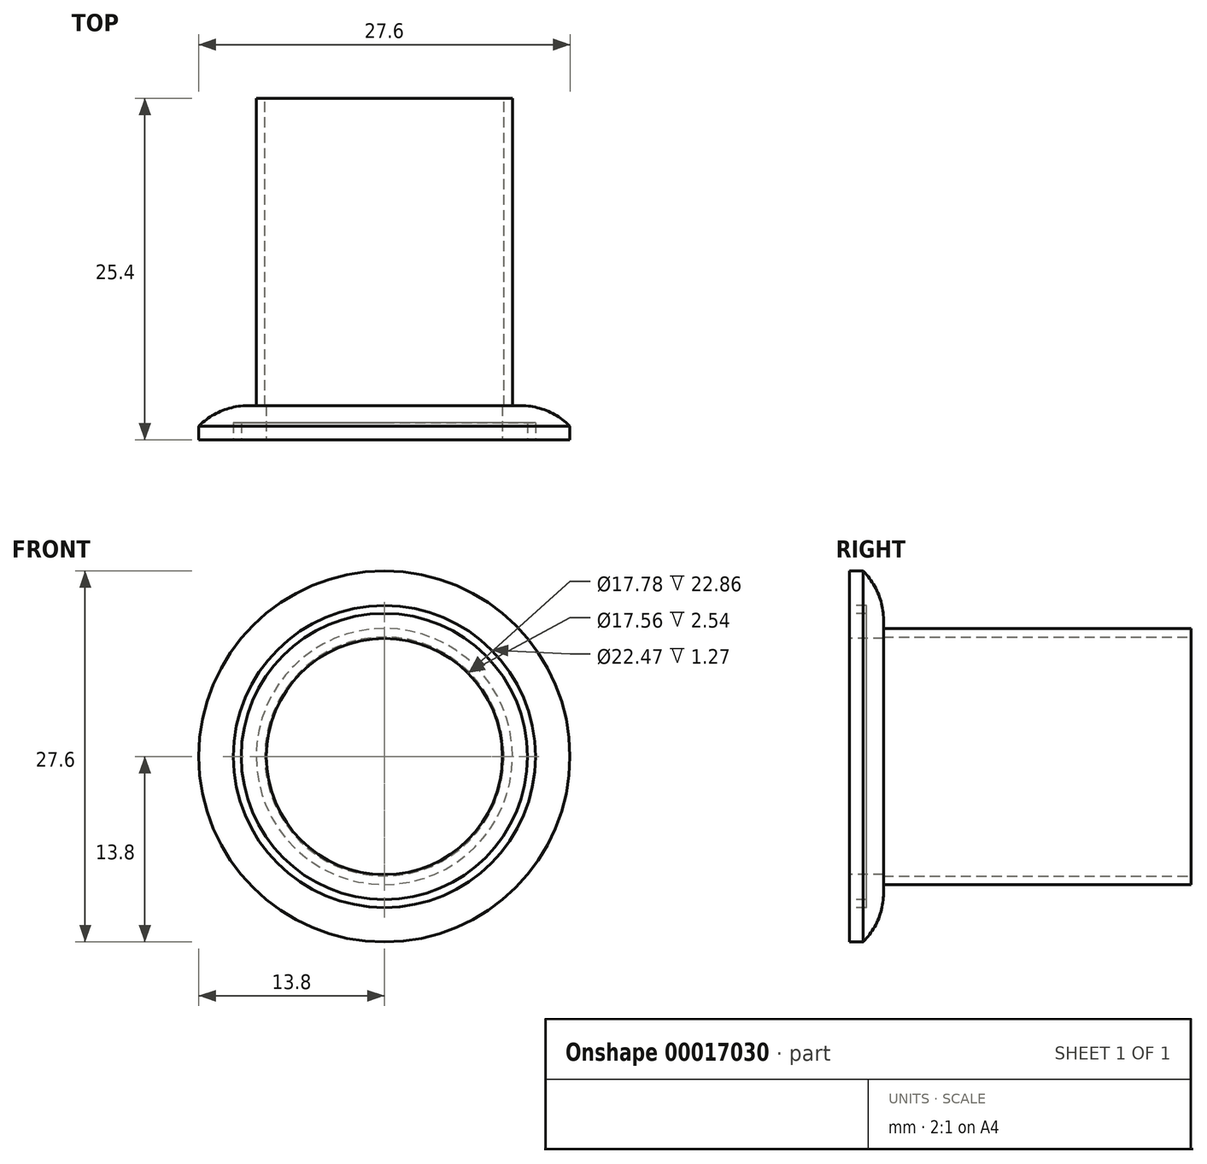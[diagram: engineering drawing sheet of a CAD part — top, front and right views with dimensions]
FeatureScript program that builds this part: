
annotation { "Feature Type Name" : "Feature", "Feature Type Description" : "" }
export const myFeature = defineFeature(function(context is Context, id is Id, definition is map)
    precondition{}
    {
        {
            var Q0;
            Q0=qCreatedBy(makeId("Front.planeOp"),FACE);
            var sketch = newSketch(context, id + "F0", { "sketchPlane" : qUnion([Q0])});
            skCircle(sketch, "E0", {"center": v(0, 0) * mm, "radius": 9.53 * mm});
            skCircle(sketch, "E1", {"center": v(0, 0) * mm, "radius": 8.9 * mm});
            skSolve(sketch);
        }
        {
            var Q0;
            Q0 = qSketchRegion(id + "F0", true);
            extrude(context, id + "F1", {"entities" : qUnion([Q0]), "depth" : 25.4 * mm});
        }
        {
            var Q0;
            Q0=makeQuery(id+"F1.opExtrude","CAP_FACE",FACE,{"disambiguationData":[OSD([sQuery(id+"F0.wireOp",EDGE,"E0"),sQuery(id+"F0.wireOp",EDGE,"E1")])],"isStart":false});
            var sketch = newSketch(context, id + "F2", { "sketchPlane" : qUnion([Q0])});
            skCircle(sketch, "E2", {"center": v(0, 0) * mm, "radius": 13.8 * mm});
            skCircle(sketch, "E3", {"center": v(0, 0) * mm, "radius": 8.78 * mm});
            skSolve(sketch);
        }
        {
            var Q0;
            Q0 = qSketchRegion(id + "F2", true);
            extrude(context, id + "F3", {"entities" : qUnion([Q0]), "operationType" : NewBodyOperationType.ADD, "oppositeDirection" : true, "depth" : 2.54 * mm});
        }
        {
            var Q0;
            Q0=makeQuery(id+"F3.opExtrude","CAP_EDGE",EDGE,{"disambiguationData":[OSD([sQuery(id+"F2.wireOp",EDGE,"E2")])],"isStart":false});
            chamfer(context, id + "F4", {"entities" : qUnion([Q0]), "width" : 1.52 * mm, "tangentPropagation" : true});
        }
        {
            var Q0;
            {var subQ0=sQuery(id+"F2.wireOp",EDGE,"E2");Q0=makeQuery(id+"F4.opChamfer","BLEND_EDGE",EDGE,{"blendedFrom":[makeQuery(id+"F3.opExtrude","CAP_EDGE",EDGE,{"disambiguationData":[OSD([subQ0])],"isStart":false}),makeQuery(id+"F3.boolean.opBoolean","SPLIT",FACE,{"disambiguationData":[TD([makeQuery(id+"F1.opExtrude","SWEPT_FACE",FACE,{"disambiguationData":[OSD([sQuery(id+"F0.wireOp",EDGE,"E0")])]})])],"derivedFrom":makeQuery(id+"F3.opExtrude","CAP_FACE",FACE,{"disambiguationData":[OSD([subQ0,sQuery(id+"F2.wireOp",EDGE,"E3")])],"isStart":false})})],"blendedInto":[makeQuery(id+"F3.boolean.opBoolean","SPLIT",FACE,{"disambiguationData":[TD([makeQuery(id+"F1.opExtrude","SWEPT_FACE",FACE,{"disambiguationData":[OSD([sQuery(id+"F0.wireOp",EDGE,"E0")])]})])],"derivedFrom":makeQuery(id+"F3.opExtrude","CAP_FACE",FACE,{"disambiguationData":[OSD([subQ0,sQuery(id+"F2.wireOp",EDGE,"E3")])],"isStart":false})})]});}
            fillet(context, id + "F5", {"entities" : qUnion([Q0]), "radius" : 5.08 * mm, "tangentPropagation" : true, "allowEdgeOverflow" : false});
        }
        {
            var Q0;
            Q0=makeQuery(id+"F3.boolean.opBoolean","MERGE",FACE,{"derivedFrom":[makeQuery(id+"F1.opExtrude","CAP_FACE",FACE,{"disambiguationData":[OSD([sQuery(id+"F0.wireOp",EDGE,"E0"),sQuery(id+"F0.wireOp",EDGE,"E1")])],"isStart":false}),makeQuery(id+"F3.opExtrude","CAP_FACE",FACE,{"disambiguationData":[OSD([sQuery(id+"F2.wireOp",EDGE,"E2"),sQuery(id+"F2.wireOp",EDGE,"E3")])],"isStart":true})]});
            var sketch = newSketch(context, id + "F6", { "sketchPlane" : qUnion([Q0])});
            skCircle(sketch, "E4", {"center": v(0, 0) * mm, "radius": 11.23 * mm});
            skCircle(sketch, "E5", {"center": v(0, 0) * mm, "radius": 10.64 * mm});
            skSolve(sketch);
        }
        {
            var Q0;
            Q0 = qSketchRegion(id + "F6", true);
            extrude(context, id + "F7", {"entities" : qUnion([Q0]), "operationType" : NewBodyOperationType.REMOVE, "oppositeDirection" : true, "depth" : 1.27 * mm});
        }
    });
